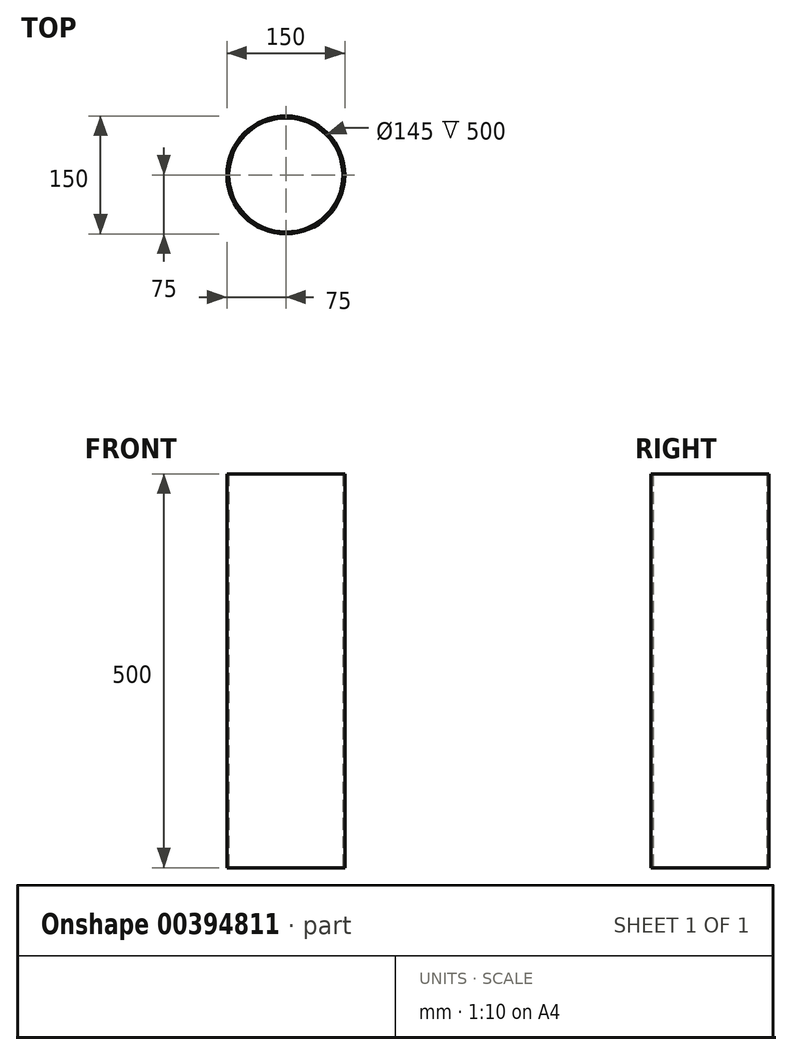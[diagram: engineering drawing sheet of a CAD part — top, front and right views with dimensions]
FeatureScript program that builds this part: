
annotation { "Feature Type Name" : "Feature", "Feature Type Description" : "" }
export const myFeature = defineFeature(function(context is Context, id is Id, definition is map)
    precondition{}
    {
        {
            var Q0;
            Q0=qCreatedBy(makeId("Top.planeOp"),FACE);
            var sketch = newSketch(context, id + "F0", { "sketchPlane" : qUnion([Q0])});
            skCircle(sketch, "E0", {"center": v(0, 0) * mm, "radius": 75 * mm});
            skCircle(sketch, "E1", {"center": v(0, 0) * mm, "radius": 72.5 * mm});
            skSolve(sketch);
        }
        {
            var Q0;
            Q0=makeQuery(id+"F0.imprint","IMPRINT",FACE,{"disambiguationData":[TD([[makeQuery(id+"F0.imprint","IMPRINT",EDGE,{"derivedFrom":sQuery(id+"F0.wireOp",EDGE,"E0")}),1.0]])]});
            extrude(context, id + "F1", {"entities" : qUnion([Q0]), "depth" : 500 * mm});
        }
    });
